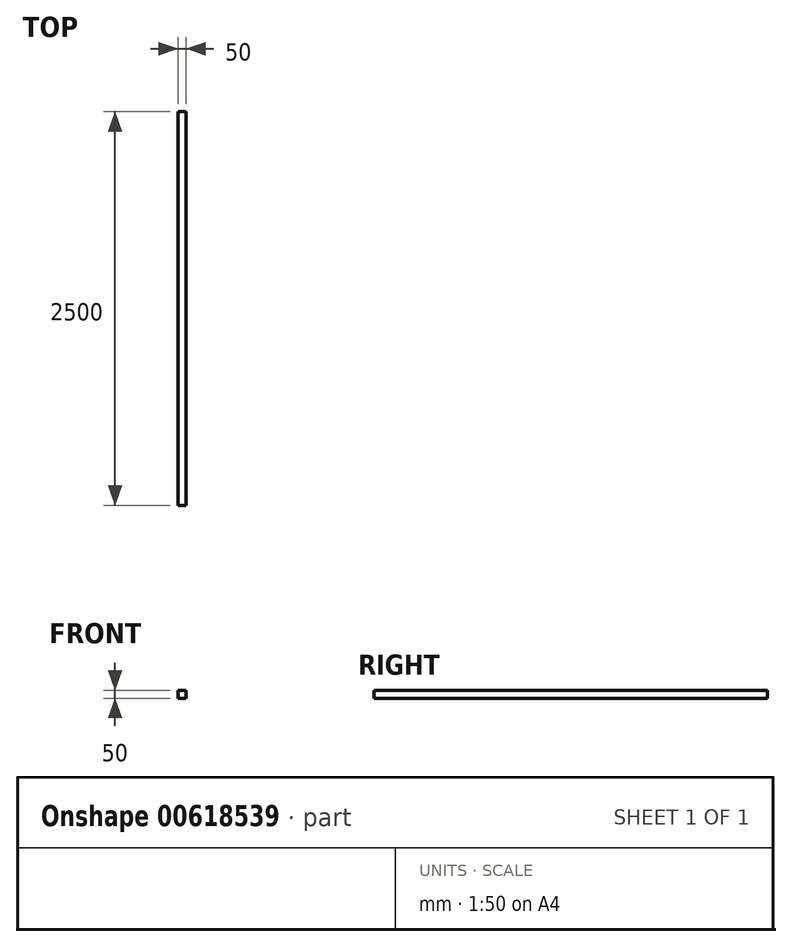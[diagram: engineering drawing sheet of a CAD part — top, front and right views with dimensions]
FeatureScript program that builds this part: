
annotation { "Feature Type Name" : "Feature", "Feature Type Description" : "" }
export const myFeature = defineFeature(function(context is Context, id is Id, definition is map)
    precondition{}
    {
        {
            var Q0;
            Q0=qCreatedBy(makeId("Front.planeOp"),FACE);
            var sketch = newSketch(context, id + "F0", { "sketchPlane" : qUnion([Q0])});
            skLineSegment(sketch, "E0.bottom", {"start": v(-25.64, -26.89) * mm, "end": v(24.36, -26.89) * mm});
            skLineSegment(sketch, "E0.top", {"start": v(-25.64, 23.11) * mm, "end": v(24.36, 23.11) * mm});
            skLineSegment(sketch, "E0.left", {"start": v(-25.64, -26.89) * mm, "end": v(-25.64, 23.11) * mm});
            skLineSegment(sketch, "E0.right", {"start": v(24.36, -26.89) * mm, "end": v(24.36, 23.11) * mm});
            skSolve(sketch);
        }
        {
            var Q0;
            Q0=makeQuery(id+"F0.imprint","IMPRINT",FACE,{"disambiguationData":[TD([[makeQuery(id+"F0.imprint","IMPRINT",EDGE,{"derivedFrom":sQuery(id+"F0.wireOp",EDGE,"E0.bottom")}),1.0]])]});
            extrude(context, id + "F1", {"entities" : qUnion([Q0]), "depth" : 2500 * mm, "offsetDistance" : 25 * mm});
        }
    });
